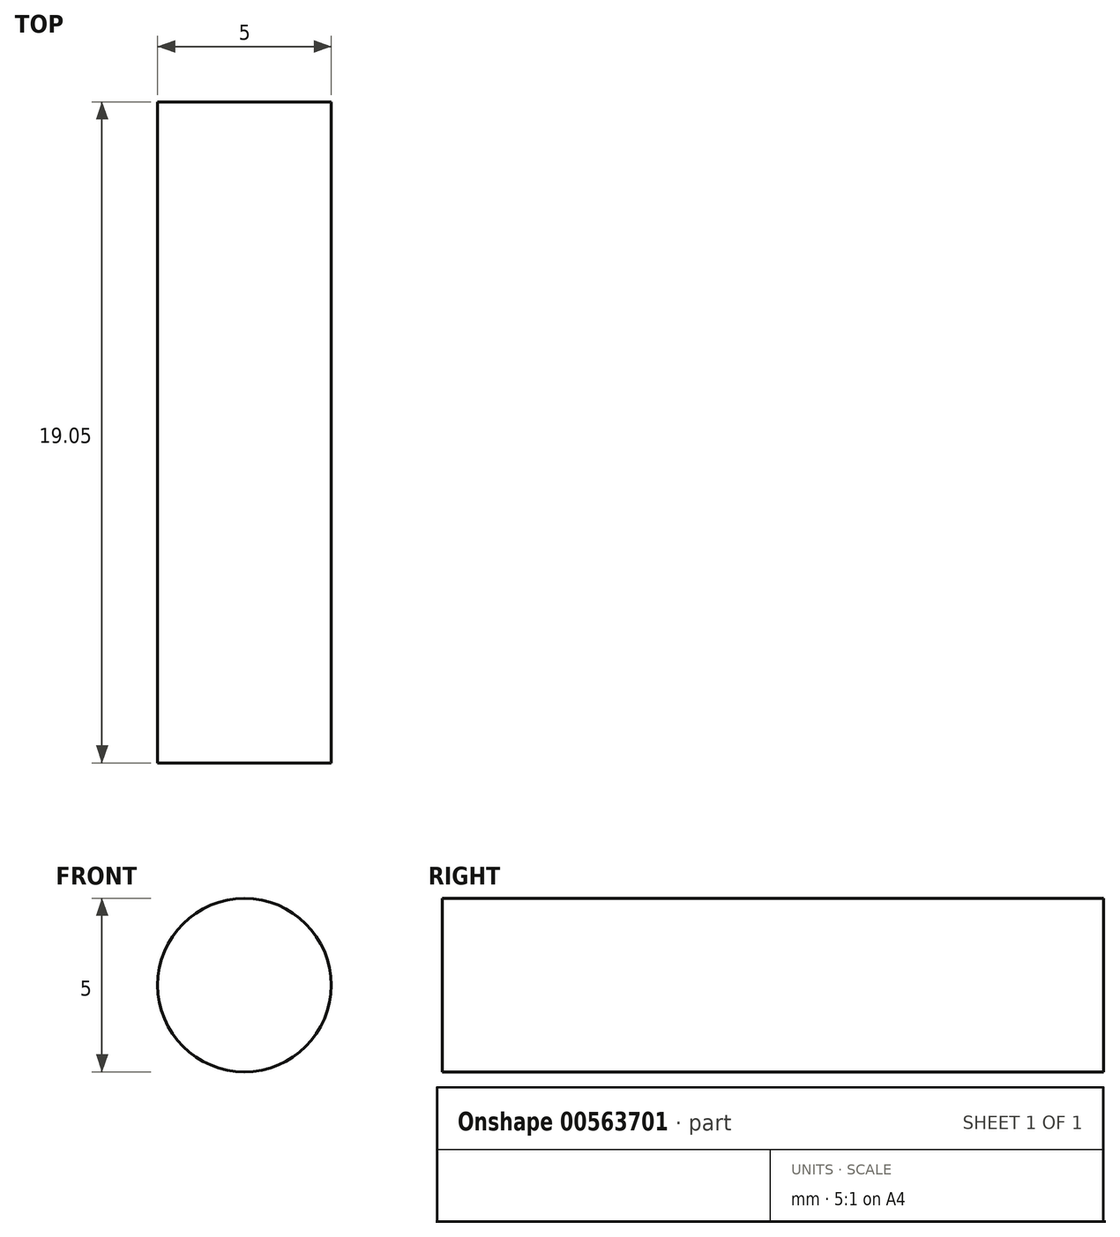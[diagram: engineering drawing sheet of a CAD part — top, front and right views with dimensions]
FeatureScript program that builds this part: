
annotation { "Feature Type Name" : "Feature", "Feature Type Description" : "" }
export const myFeature = defineFeature(function(context is Context, id is Id, definition is map)
    precondition{}
    {
        {
            var Q0;
            Q0=qCreatedBy(makeId("Front.planeOp"),FACE);
            var sketch = newSketch(context, id + "F0", { "sketchPlane" : qUnion([Q0])});
            skCircle(sketch, "E0", {"center": v(0, 0) * mm, "radius": 2.5 * mm});
            skSolve(sketch);
        }
        {
            var Q0;
            Q0 = qSketchRegion(id + "F0", true);
            extrude(context, id + "F1", {"entities" : qUnion([Q0]), "depth" : 19.05 * mm, "offsetDistance" : 25.4 * mm});
        }
    });
